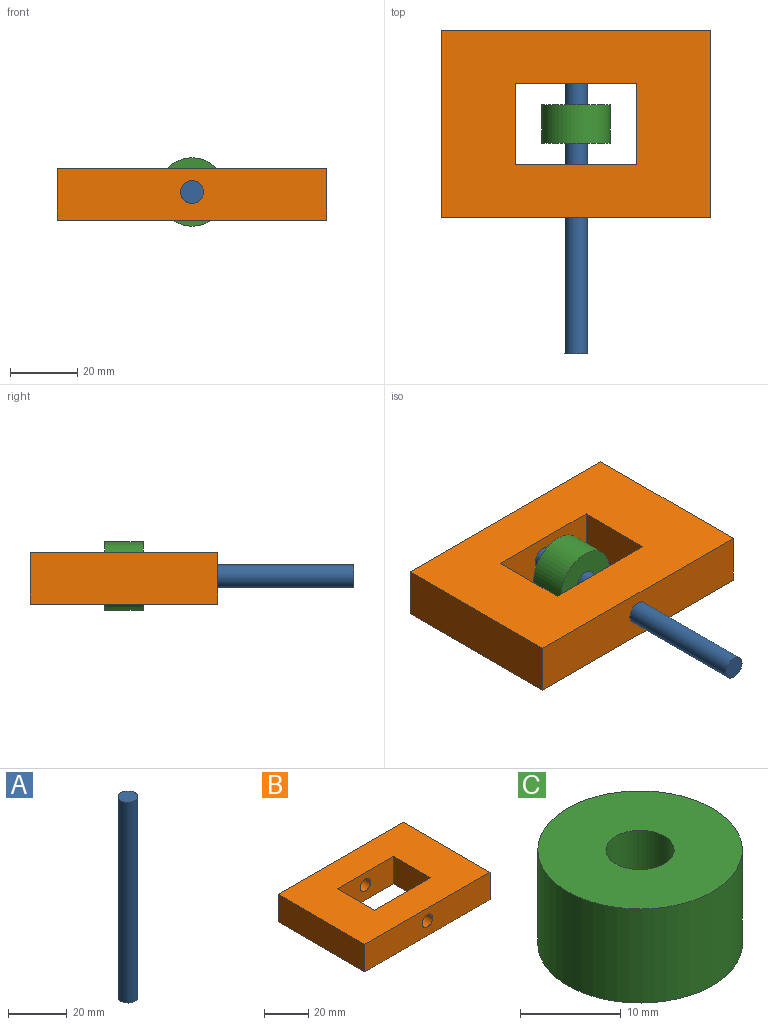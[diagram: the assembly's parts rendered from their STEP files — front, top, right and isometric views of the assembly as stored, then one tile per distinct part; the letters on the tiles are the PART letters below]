
ASSEMBLY  parts=3 mates=2
PART A: 3 faces, bbox 6.8x6.8x83.6 mm
  f0: cylinder r=3.38mm len=83.57mm, axis (0,0,-1), area 1777.3mm2, adj f1,f2
  f1: plane 6.77x6.77mm, normal (0,0,1), area 36mm2, adj f0
  f2: plane 6.77x6.77mm, normal (0,0,-1), area 36mm2, adj f0
PART B: 13 faces, bbox 80.3x55.8x15.2 mm
  f0: plane 80.26x15.24mm, normal (0,1,0), area 1223.1mm2, adj f1,f7,f8,f9
  f1: plane 55.82x15.24mm, normal (-1,0,0), area 850.7mm2, adj f0,f2,f8,f9
  f2: plane 80.26x15.24mm, normal (0,-1,0), area 1187.1mm2, adj f1,f7,f8,f9,f10
  f3: plane 23.93x15.24mm, normal (1,0,0), area 364.7mm2, adj f4,f6,f8,f9
  f4: plane 36.1x15.24mm, normal (0,-1,0), area 514.2mm2, adj f3,f5,f8,f9,f11
  f5: plane 23.93x15.24mm, normal (-1,0,0), area 364.7mm2, adj f4,f6,f8,f9
  f6: plane 36.1x15.24mm, normal (0,1,0), area 514.2mm2, adj f3,f5,f8,f9,f10
  f7: plane 55.82x15.24mm, normal (1,0,0), area 850.7mm2, adj f0,f2,f8,f9
  f8: plane 80.26x55.82mm, normal (0,0,1), area 3615.9mm2, adj f0,f1,f2,f3,f4,f5,f6,f7
  f9: plane 80.26x55.82mm, normal (0,0,-1), area 3615.9mm2, adj f0,f1,f2,f3,f4,f5,f6,f7
  f10: cylinder r=3.38mm len=15.94mm, axis (0,-1,0), area 339.1mm2, adj f2,f6
  f11: cylinder r=3.38mm len=6.77mm, axis (0,-1,0), area 140.5mm2, adj f4,f12
  f12: plane 6.77x6.77mm, normal (0,-1,0), area 36mm2, adj f11
PART C: 4 faces, bbox 20.3x20.3x11.4 mm
  f0: cylinder r=3.38mm len=11.43mm, axis (0,0,-1), area 243.1mm2, adj f2,f3
  f1: cylinder r=10.16mm len=20.32mm, axis (0,0,-1), area 729.7mm2, adj f2,f3
  f2: plane 20.32x20.32mm, normal (0,0,1), area 288.3mm2, adj f0,f1
  f3: plane 20.32x20.32mm, normal (0,0,-1), area 288.3mm2, adj f0,f1
PLACE A rot(axis=(-1,0,0),90deg) t=(-12.93,-69.96,16.21)mm
PLACE B t=(-12.93,-1.66,7.86)mm
PLACE C rot(axis=(-1,0,0),90deg) t=(-12.93,-7.31,16.21)mm
MATE slider A.f0 <-> C.f0  axis (0,-1,0) through (-12.93,-28.17,16.21)mm
MATE fastened A.f0 <-> B.f10  axis (0,1,0) through (-12.93,13.61,16.21)mm
